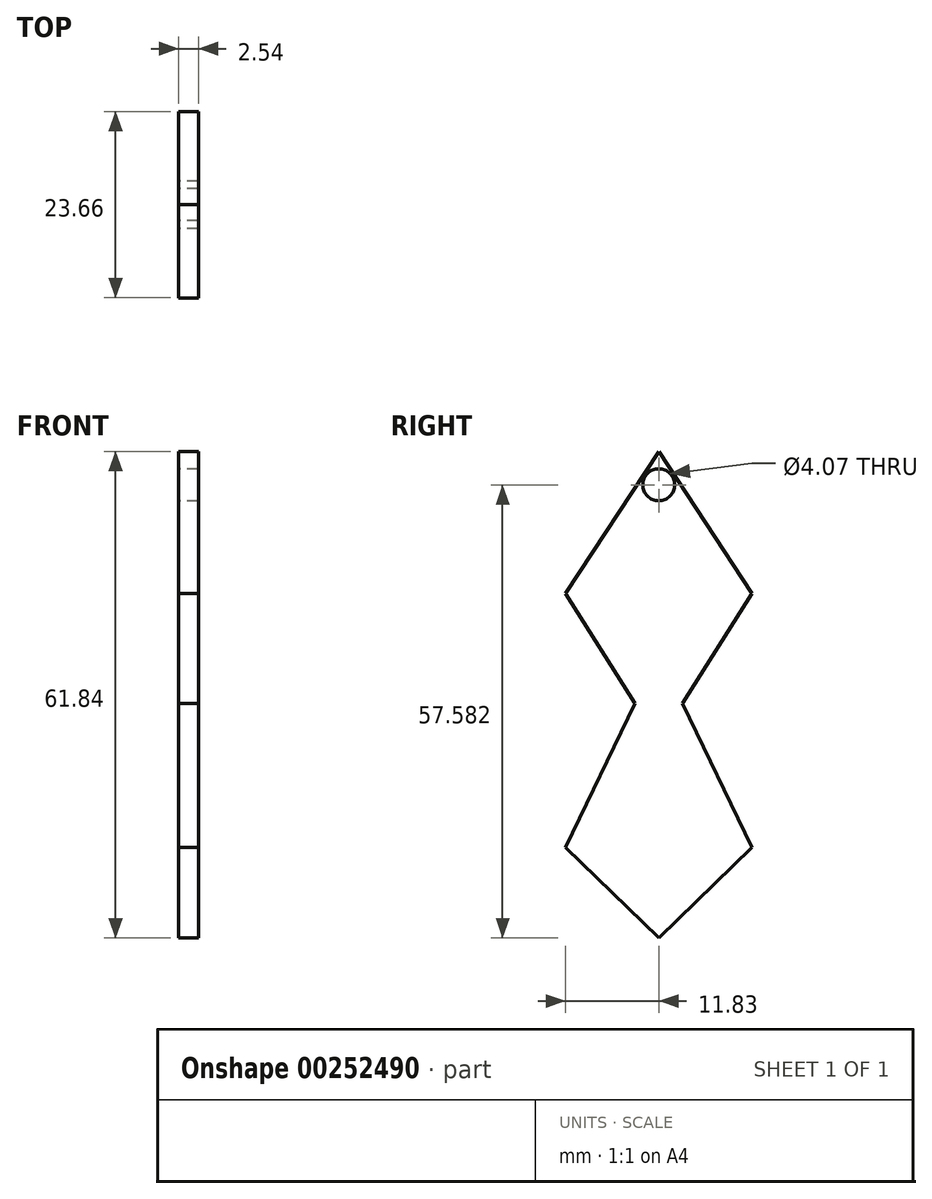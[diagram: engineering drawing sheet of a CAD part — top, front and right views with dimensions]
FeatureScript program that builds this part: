
annotation { "Feature Type Name" : "Feature", "Feature Type Description" : "" }
export const myFeature = defineFeature(function(context is Context, id is Id, definition is map)
    precondition{}
    {
        {
            var Q0;
            Q0=qCreatedBy(makeId("Right.planeOp"),FACE);
            var sketch = newSketch(context, id + "F0", { "sketchPlane" : qUnion([Q0])});
            skLineSegment(sketch, "E0", {"start": v(0, 24.13) * mm, "end": v(-11.83, 6.07) * mm});
            skLineSegment(sketch, "E1", {"start": v(-11.83, 6.07) * mm, "end": v(-3.02, -7.89) * mm});
            skLineSegment(sketch, "E2", {"start": v(-3.02, -7.89) * mm, "end": v(-11.83, -26.2) * mm});
            skLineSegment(sketch, "E3", {"start": v(-11.83, -26.2) * mm, "end": v(0, -37.7) * mm});
            skLineSegment(sketch, "E4", {"start": v(0, -37.7) * mm, "end": v(11.83, -26.2) * mm});
            skLineSegment(sketch, "E5", {"start": v(11.83, -26.2) * mm, "end": v(3.02, -7.89) * mm});
            skLineSegment(sketch, "E6", {"start": v(3.02, -7.89) * mm, "end": v(11.83, 6.07) * mm});
            skLineSegment(sketch, "E7", {"start": v(11.83, 6.07) * mm, "end": v(0, 24.13) * mm});
            skCircle(sketch, "E8", {"center": v(0, 19.87) * mm, "radius": 2.03 * mm});
            skSolve(sketch);
        }
        {
            var Q0;
            Q0=makeQuery(id+"F0.imprint","IMPRINT",FACE,{"disambiguationData":[TD([[makeQuery(id+"F0.imprint","IMPRINT",EDGE,{"derivedFrom":sQuery(id+"F0.wireOp",EDGE,"E0")}),1.0]])]});
            extrude(context, id + "F1", {"entities" : qUnion([Q0]), "depth" : 2.54 * mm});
        }
    });
